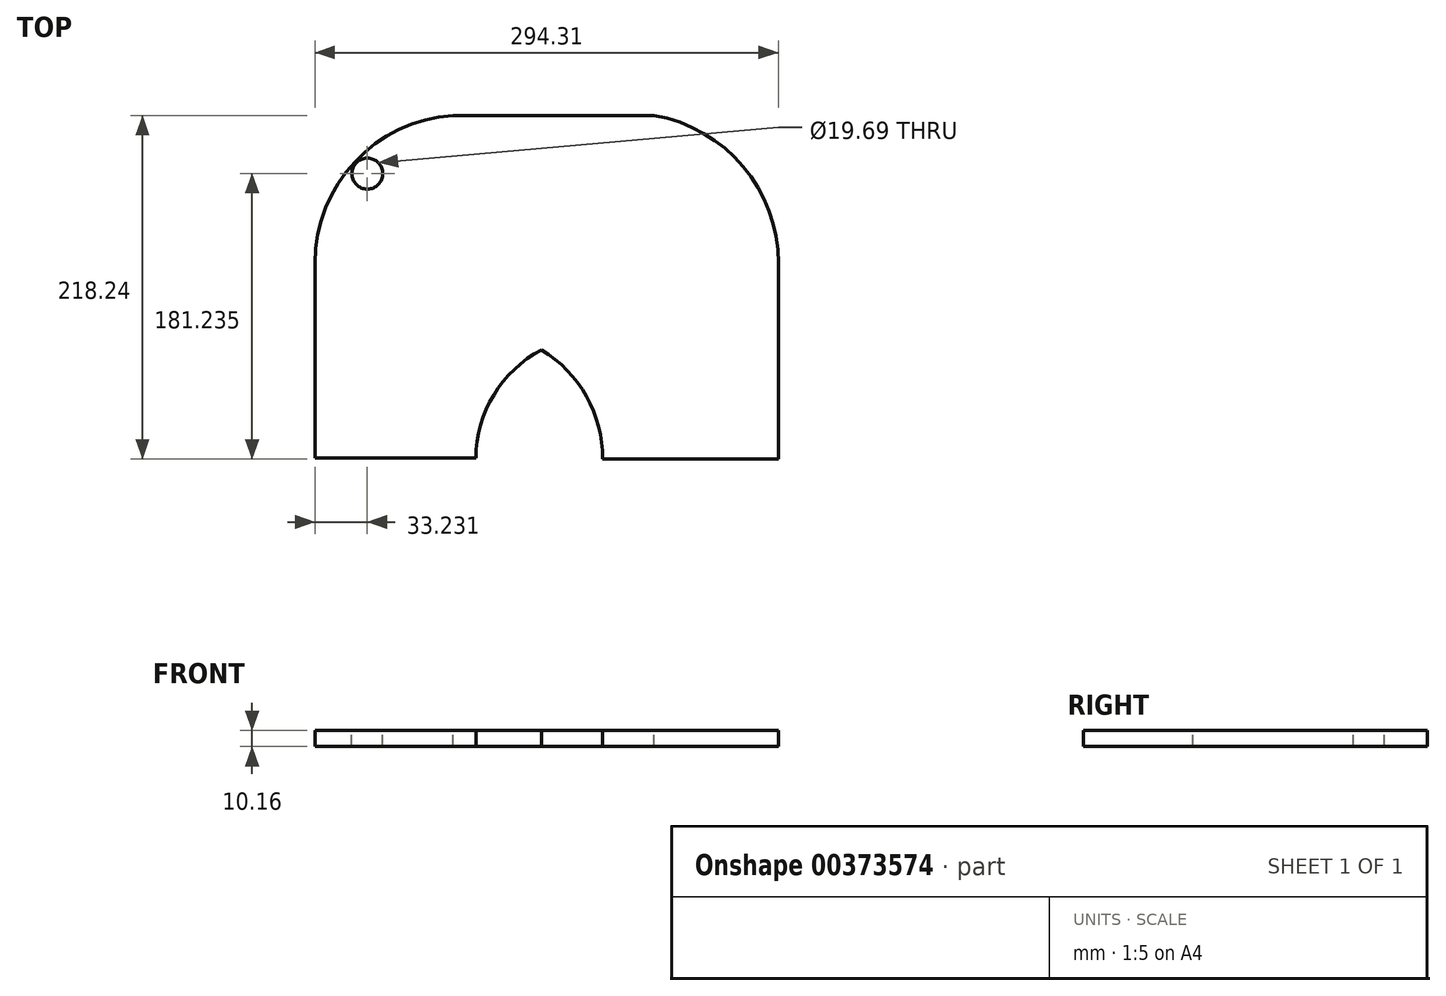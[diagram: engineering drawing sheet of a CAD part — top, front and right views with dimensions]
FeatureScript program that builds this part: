
annotation { "Feature Type Name" : "Feature", "Feature Type Description" : "" }
export const myFeature = defineFeature(function(context is Context, id is Id, definition is map)
    precondition{}
    {
        {
            var Q0;
            Q0=qCreatedBy(makeId("Top.planeOp"),FACE);
            var sketch = newSketch(context, id + "F0", { "sketchPlane" : qUnion([Q0])});
            skLineSegment(sketch, "E0.bottom", {"start": v(-143.91, 55.14) * mm, "end": v(150.4, 55.14) * mm});
            skLineSegment(sketch, "E0.left", {"start": v(-143.91, 55.14) * mm, "end": v(-143.91, -68.78) * mm});
            skLineSegment(sketch, "E0.right", {"start": v(150.4, 55.14) * mm, "end": v(150.4, -69.31) * mm});
            skLineSegment(sketch, "E1", {"start": v(-143.91, -68.78) * mm, "end": v(-41.5, -68.78) * mm});
            skLineSegment(sketch, "E2", {"start": v(150.4, -69.31) * mm, "end": v(36.77, -69.31) * mm});
            skArc(sketch, "E3", {"start": v(0, 0) * mm, "mid": v(28.52, -29.54) * mm, "end": v(38.74, -69.31) * mm});
            skArc(sketch, "E4", {"start": v(0, 0) * mm, "mid": v(-30.33, -28.64) * mm, "end": v(-41.69, -68.78) * mm});
            skLineSegment(sketch, "E5.bottom", {"start": v(71.39, 55.14) * mm, "end": v(-56.14, 55.14) * mm});
            skLineSegment(sketch, "E5.top", {"start": v(71.39, 148.93) * mm, "end": v(-56.14, 148.93) * mm});
            skLineSegment(sketch, "E5.left", {"start": v(71.39, 55.14) * mm, "end": v(71.39, 148.93) * mm});
            skLineSegment(sketch, "E5.right", {"start": v(-56.14, 55.14) * mm, "end": v(-56.14, 148.93) * mm});
            skArc(sketch, "E6", {"start": v(-143.91, 55.14) * mm, "mid": v(-118.55, 119.37) * mm, "end": v(-56.14, 148.93) * mm});
            skArc(sketch, "E7", {"start": v(150.4, 55.14) * mm, "mid": v(128.01, 116.46) * mm, "end": v(71.39, 148.93) * mm});
            skLineSegment(sketch, "E8", {"start": v(-126.3, 109.92) * mm, "end": v(-135.32, 255.14) * mm});
            skCircle(sketch, "E9", {"center": v(-110.68, 111.92) * mm, "radius": 9.85 * mm});
            skSolve(sketch);
        }
        {
            var Q0;
            Q0 = qSketchRegion(id + "F0", true);
            extrude(context, id + "F1", {"entities" : qUnion([Q0]), "oppositeDirection" : true, "depth" : 10.16 * mm});
        }
    });
